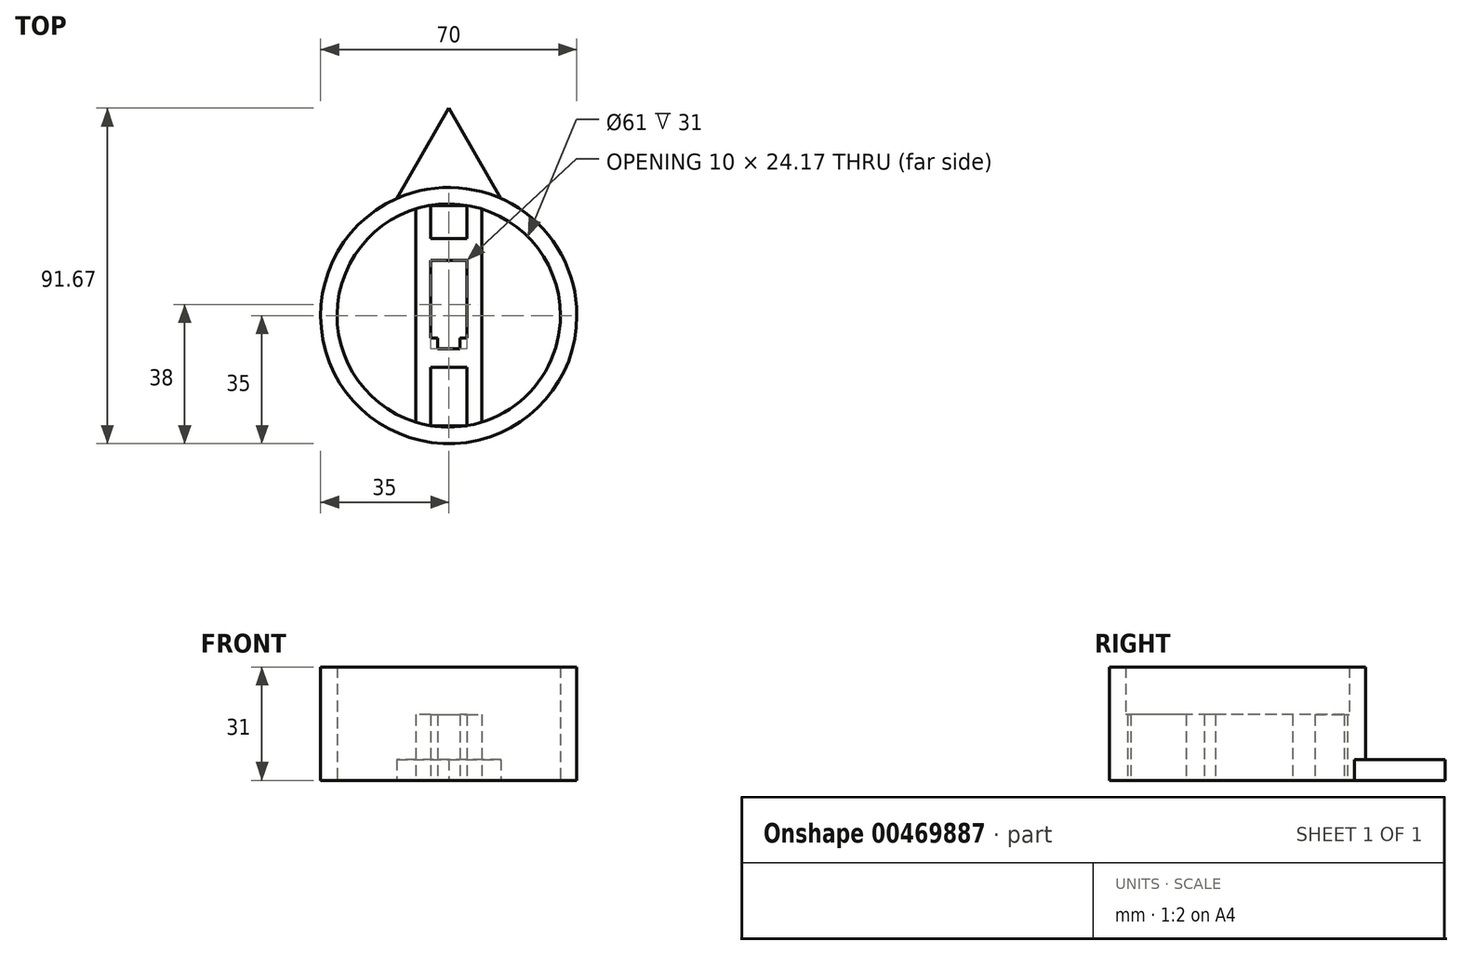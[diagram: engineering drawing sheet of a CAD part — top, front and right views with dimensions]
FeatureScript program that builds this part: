
annotation { "Feature Type Name" : "Feature", "Feature Type Description" : "" }
export const myFeature = defineFeature(function(context is Context, id is Id, definition is map)
    precondition{}
    {
        {
            var Q0;
            Q0=qCreatedBy(makeId("Top.planeOp"),FACE);
            var sketch = newSketch(context, id + "F0", { "sketchPlane" : qUnion([Q0])});
            skCircle(sketch, "E0", {"center": v(0, 0) * mm, "radius": 35 * mm});
            skCircle(sketch, "E1", {"center": v(0, 0) * mm, "radius": 30.5 * mm});
            skLineSegment(sketch, "E2", {"start": v(-5, 30.09) * mm, "end": v(-5, -30.09) * mm});
            skLineSegment(sketch, "E3", {"start": v(-5, -30.09) * mm, "end": v(5, -30.09) * mm});
            skLineSegment(sketch, "E4", {"start": v(5, -30.09) * mm, "end": v(5, 30.09) * mm});
            skLineSegment(sketch, "E5", {"start": v(5, 30.09) * mm, "end": v(-5, 30.09) * mm});
            skLineSegment(sketch, "E6", {"start": v(5, 30.09) * mm, "end": v(9, 30.09) * mm});
            skLineSegment(sketch, "E7", {"start": v(9, 30.09) * mm, "end": v(9, -30.09) * mm});
            skLineSegment(sketch, "E8", {"start": v(9, -30.09) * mm, "end": v(5, -30.29) * mm});
            skLineSegment(sketch, "E9", {"start": v(-5, 30.09) * mm, "end": v(-9, 30.09) * mm});
            skLineSegment(sketch, "E10", {"start": v(-9, 30.09) * mm, "end": v(-9, -30.09) * mm});
            skLineSegment(sketch, "E11", {"start": v(-9, -30.09) * mm, "end": v(-5, -30.09) * mm});
            skLineSegment(sketch, "E12", {"start": v(0, 21.09) * mm, "end": v(-5, 21.09) * mm});
            skLineSegment(sketch, "E13", {"start": v(-5, 21.09) * mm, "end": v(5, 21.09) * mm});
            skLineSegment(sketch, "E14", {"start": v(0, 15.09) * mm, "end": v(-5, 15.09) * mm});
            skLineSegment(sketch, "E15", {"start": v(-5, 15.09) * mm, "end": v(5, 15.09) * mm});
            skLineSegment(sketch, "E16", {"start": v(0, -14.09) * mm, "end": v(-5, -14.09) * mm});
            skLineSegment(sketch, "E17", {"start": v(-5, -14.09) * mm, "end": v(5, -14.09) * mm});
            skPoint(sketch, "E17.endSnap0", {"position": v(-2.5, -14.09) * mm});
            skLineSegment(sketch, "E18", {"start": v(0, -9.09) * mm, "end": v(-5, -9.09) * mm});
            skLineSegment(sketch, "E19", {"start": v(-5, -9.09) * mm, "end": v(5, -9.09) * mm});
            skLineSegment(sketch, "E20", {"start": v(-5, -6.09) * mm, "end": v(-3, -6.09) * mm});
            skLineSegment(sketch, "E21", {"start": v(-3, -6.09) * mm, "end": v(-3, -9.09) * mm});
            skLineSegment(sketch, "E22", {"start": v(5, -6.09) * mm, "end": v(3, -6.09) * mm});
            skLineSegment(sketch, "E23", {"start": v(3, -6.09) * mm, "end": v(3, -9.09) * mm});
            skSolve(sketch);
        }
        {
            var Q0;
            Q0=makeQuery(id+"F0.imprint","IMPRINT",FACE,{"disambiguationData":[TD([[makeQuery(id+"F0.imprint","IMPRINT",EDGE,{"derivedFrom":sQuery(id+"F0.wireOp",EDGE,"E0")}),1.0]])]});
            var Q1;
            {var subQ0=sQuery(id+"F0.wireOp",EDGE,"E2");var subQ3=makeQuery(id+"F0.imprint","INTERSECT",VERTEX,{"derivedFrom":[subQ0,sQuery(id+"F0.wireOp",EDGE,"E13")]});Q1=makeQuery(id+"F0.imprint","IMPRINT",FACE,{"disambiguationData":[TD([[makeQuery(id+"F0.imprint","IMPRINT",EDGE,{"disambiguationData":[TD([[subQ3,-1.0]])],"derivedFrom":subQ0}),-1.0]])]});}
            var Q2;
            {var subQ0=sQuery(id+"F0.wireOp",EDGE,"E9");Q2=makeQuery(id+"F0.imprint","IMPRINT",FACE,{"disambiguationData":[TD([[makeQuery(id+"F0.imprint","IMPRINT",EDGE,{"derivedFrom":subQ0}),1.0]])]});}
            var Q3;
            {var subQ0=sQuery(id+"F0.wireOp",EDGE,"E5");Q3=makeQuery(id+"F0.imprint","IMPRINT",FACE,{"disambiguationData":[TD([[makeQuery(id+"F0.imprint","IMPRINT",EDGE,{"derivedFrom":subQ0}),-1.0]])]});}
            var Q4;
            {var subQ0=sQuery(id+"F0.wireOp",EDGE,"E6");Q4=makeQuery(id+"F0.imprint","IMPRINT",FACE,{"disambiguationData":[TD([[makeQuery(id+"F0.imprint","IMPRINT",EDGE,{"derivedFrom":subQ0}),-1.0]])]});}
            var Q5;
            {var subQ0=sQuery(id+"F0.wireOp",EDGE,"E4");var subQ1=makeQuery(id+"F0.imprint","INTERSECT",VERTEX,{"derivedFrom":[subQ0,sQuery(id+"F0.wireOp",EDGE,"E17")]});Q5=makeQuery(id+"F0.imprint","IMPRINT",FACE,{"disambiguationData":[TD([[makeQuery(id+"F0.imprint","IMPRINT",EDGE,{"disambiguationData":[TD([[subQ1,-1.0]])],"derivedFrom":subQ0}),-1.0]])]});}
            var Q6;
            {var subQ0=sQuery(id+"F0.wireOp",EDGE,"E13");var subQ3=makeQuery(id+"F0.imprint","IMPRINT",VERTEX,{"derivedFrom":subQ0});Q6=makeQuery(id+"F0.imprint","IMPRINT",FACE,{"disambiguationData":[TD([[makeQuery(id+"F0.imprint","IMPRINT",EDGE,{"disambiguationData":[TD([[subQ3,1.0]])],"derivedFrom":subQ0}),-1.0]])]});}
            var Q7;
            {var subQ3=sQuery(id+"F0.wireOp",EDGE,"E20");Q7=makeQuery(id+"F0.imprint","IMPRINT",FACE,{"disambiguationData":[TD([[makeQuery(id+"F0.imprint","IMPRINT",EDGE,{"derivedFrom":subQ3}),-1.0]])]});}
            var Q8;
            {var subQ3=sQuery(id+"F0.wireOp",EDGE,"E22");Q8=makeQuery(id+"F0.imprint","IMPRINT",FACE,{"disambiguationData":[TD([[makeQuery(id+"F0.imprint","IMPRINT",EDGE,{"derivedFrom":subQ3}),1.0]])]});}
            var Q9;
            {var subQ0=sQuery(id+"F0.wireOp",EDGE,"E17");var subQ3=makeQuery(id+"F0.imprint","IMPRINT",VERTEX,{"derivedFrom":subQ0});Q9=makeQuery(id+"F0.imprint","IMPRINT",FACE,{"disambiguationData":[TD([[makeQuery(id+"F0.imprint","IMPRINT",EDGE,{"disambiguationData":[TD([[subQ3,1.0]])],"derivedFrom":subQ0}),1.0]])]});}
            var Q10;
            {var subQ0=sQuery(id+"F0.wireOp",EDGE,"E3");Q10=makeQuery(id+"F0.imprint","IMPRINT",FACE,{"disambiguationData":[TD([[makeQuery(id+"F0.imprint","IMPRINT",EDGE,{"derivedFrom":subQ0}),-1.0]])]});}
            var Q11;
            {var subQ0=sQuery(id+"F0.wireOp",EDGE,"E11");Q11=makeQuery(id+"F0.imprint","IMPRINT",FACE,{"disambiguationData":[TD([[makeQuery(id+"F0.imprint","IMPRINT",EDGE,{"derivedFrom":subQ0}),1.0]])]});}
            extrude(context, id + "F1", {"entities" : qUnion([Q0, Q1, Q2, Q3, Q4, Q5, Q6, Q7, Q8, Q9, Q10, Q11]), "depth" : 18 * mm});
        }
        {
            var Q0;
            Q0=qCreatedBy(makeId("Top.planeOp"),FACE);
            var sketch = newSketch(context, id + "F2", { "sketchPlane" : qUnion([Q0])});
            skCircle(sketch, "E24", {"center": v(0, 0) * mm, "radius": 35 * mm});
            skCircle(sketch, "E25", {"center": v(0, 0) * mm, "radius": 30.5 * mm});
            skSolve(sketch);
        }
        {
            var Q0;
            Q0=makeQuery(id+"F2.imprint","IMPRINT",FACE,{"disambiguationData":[TD([[makeQuery(id+"F2.imprint","IMPRINT",EDGE,{"derivedFrom":sQuery(id+"F2.wireOp",EDGE,"E24")}),1.0]])]});
            extrude(context, id + "F3", {"entities" : qUnion([Q0]), "operationType" : NewBodyOperationType.ADD, "depth" : 31 * mm});
        }
        {
            var Q0;
            Q0=qCreatedBy(makeId("Top.planeOp"),FACE);
            var sketch = newSketch(context, id + "F4", { "sketchPlane" : qUnion([Q0])});
            skCircle(sketch, "E26", {"center": v(0, 0) * mm, "radius": 35 * mm});
            skCircle(sketch, "E27", {"center": v(0, 0) * mm, "radius": 30.5 * mm});
            skCircle(sketch, "E28.cCircle", {"center": v(0, 0) * mm, "radius": 28.33 * mm, "construction": true});
            skLineSegment(sketch, "E28.0", {"start": v(49.07, -28.33) * mm, "end": v(-49.07, -28.33) * mm});
            skLineSegment(sketch, "E28.1", {"start": v(-49.07, -28.33) * mm, "end": v(0, 56.67) * mm});
            skLineSegment(sketch, "E28.2", {"start": v(0, 56.67) * mm, "end": v(49.07, -28.33) * mm});
            skPoint(sketch, "E28.0.midPoint", {"position": v(0, -28.33) * mm});
            skSolve(sketch);
        }
        {
            var Q0;
            {var subQ0=sQuery(id+"F4.wireOp",EDGE,"E28.1");var subQ1=sQuery(id+"F4.wireOp",EDGE,"E26");var subQ2=makeQuery(id+"F4.imprint","INTERSECT",VERTEX,{"disambiguationData":[OD(0.0)],"derivedFrom":[subQ1,subQ0]});Q0=makeQuery(id+"F4.imprint","IMPRINT",FACE,{"disambiguationData":[TD([[makeQuery(id+"F4.imprint","IMPRINT",EDGE,{"disambiguationData":[TD([[subQ2,1.0]])],"derivedFrom":subQ1}),-1.0]])]});}
            extrude(context, id + "F5", {"entities" : qUnion([Q0]), "operationType" : NewBodyOperationType.ADD, "depth" : 5.7 * mm});
        }
    });
